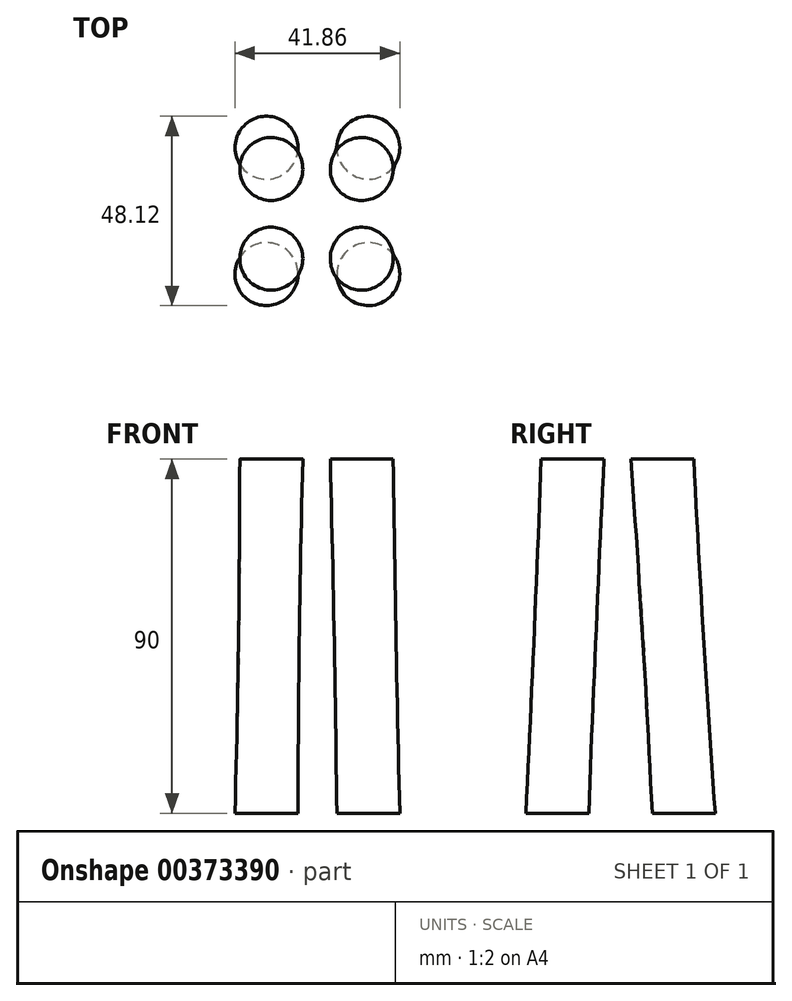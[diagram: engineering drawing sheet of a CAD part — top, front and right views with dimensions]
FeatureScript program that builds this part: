
annotation { "Feature Type Name" : "Feature", "Feature Type Description" : "" }
export const myFeature = defineFeature(function(context is Context, id is Id, definition is map)
    precondition{}
    {
        {
            var Q0;
            Q0=qCreatedBy(makeId("Top.planeOp"),FACE);
            var sketch = newSketch(context, id + "F0", { "sketchPlane" : qUnion([Q0])});
            skCircle(sketch, "E0", {"center": v(0, 0) * mm, "radius": 30 * mm});
            skPoint(sketch, "E1", {"position": v(-13.1, 16.41) * mm});
            skPoint(sketch, "E2", {"position": v(12.76, 16.41) * mm});
            skPoint(sketch, "E3", {"position": v(12.76, -15.71) * mm});
            skPoint(sketch, "E4", {"position": v(-13.1, -15.71) * mm});
            skCircle(sketch, "E5", {"center": v(-13.1, 16.41) * mm, "radius": 8 * mm});
            skCircle(sketch, "E6", {"center": v(12.76, 16.41) * mm, "radius": 8 * mm});
            skCircle(sketch, "E7", {"center": v(12.76, -15.71) * mm, "radius": 8 * mm});
            skCircle(sketch, "E8", {"center": v(-13.1, -15.71) * mm, "radius": 8 * mm});
            skSolve(sketch);
        }
        {
            var Q0;
            Q0=qCreatedBy(makeId("Top.planeOp"),FACE);
            cPlane(context, id + "F1", {"entities" : qUnion([Q0]), "cplaneType" : CPlaneType.OFFSET, "offset" : 90 * mm, "width" : 150 * mm, "height" : 150 * mm});
        }
        {
            var Q0;
            Q0=qCreatedBy(id+"F1.planeOp",FACE);
            var sketch = newSketch(context, id + "F2", { "sketchPlane" : qUnion([Q0])});
            skCircle(sketch, "E9", {"center": v(0, 0) * mm, "radius": 25 * mm});
            skPoint(sketch, "E10", {"position": v(-11.89, 11) * mm});
            skPoint(sketch, "E11", {"position": v(11.1, 11) * mm});
            skPoint(sketch, "E12", {"position": v(11.1, -11.79) * mm});
            skPoint(sketch, "E13", {"position": v(-11.89, -11.79) * mm});
            skCircle(sketch, "E14", {"center": v(-11.89, 11) * mm, "radius": 8 * mm});
            skCircle(sketch, "E15", {"center": v(11.1, 11) * mm, "radius": 8 * mm});
            skCircle(sketch, "E16", {"center": v(11.1, -11.79) * mm, "radius": 8 * mm});
            skCircle(sketch, "E17", {"center": v(-11.89, -11.79) * mm, "radius": 8 * mm});
            skSolve(sketch);
        }
        {
            var Q0;
            Q0=makeQuery(id+"F0.imprint","IMPRINT",FACE,{"disambiguationData":[TD([[makeQuery(id+"F0.imprint","IMPRINT",EDGE,{"derivedFrom":sQuery(id+"F0.wireOp",EDGE,"E7")}),1.0]])]});
            var Q1;
            Q1=makeQuery(id+"F2.imprint","IMPRINT",FACE,{"disambiguationData":[TD([[makeQuery(id+"F2.imprint","IMPRINT",EDGE,{"derivedFrom":sQuery(id+"F2.wireOp",EDGE,"E16")}),1.0]])]});
            loft(context, id + "F3", {"sheetProfilesArray" : [{ "sheetProfileEntities" : qUnion([Q0]) }, { "sheetProfileEntities" : qUnion([Q1]) }]});
        }
        {
            var Q0;
            Q0=makeQuery(id+"F0.imprint","IMPRINT",FACE,{"disambiguationData":[TD([[makeQuery(id+"F0.imprint","IMPRINT",EDGE,{"derivedFrom":sQuery(id+"F0.wireOp",EDGE,"E6")}),1.0]])]});
            var Q1;
            Q1=makeQuery(id+"F2.imprint","IMPRINT",FACE,{"disambiguationData":[TD([[makeQuery(id+"F2.imprint","IMPRINT",EDGE,{"derivedFrom":sQuery(id+"F2.wireOp",EDGE,"E15")}),1.0]])]});
            loft(context, id + "F4", {"sheetProfilesArray" : [{ "sheetProfileEntities" : qUnion([Q0]) }, { "sheetProfileEntities" : qUnion([Q1]) }]});
        }
        {
            var Q0;
            Q0=makeQuery(id+"F0.imprint","IMPRINT",FACE,{"disambiguationData":[TD([[makeQuery(id+"F0.imprint","IMPRINT",EDGE,{"derivedFrom":sQuery(id+"F0.wireOp",EDGE,"E8")}),1.0]])]});
            var Q1;
            Q1=makeQuery(id+"F2.imprint","IMPRINT",FACE,{"disambiguationData":[TD([[makeQuery(id+"F2.imprint","IMPRINT",EDGE,{"derivedFrom":sQuery(id+"F2.wireOp",EDGE,"E17")}),1.0]])]});
            loft(context, id + "F5", {"sheetProfilesArray" : [{ "sheetProfileEntities" : qUnion([Q0]) }, { "sheetProfileEntities" : qUnion([Q1]) }]});
        }
        {
            var Q0;
            Q0=makeQuery(id+"F0.imprint","IMPRINT",FACE,{"disambiguationData":[TD([[makeQuery(id+"F0.imprint","IMPRINT",EDGE,{"derivedFrom":sQuery(id+"F0.wireOp",EDGE,"E5")}),1.0]])]});
            var Q1;
            Q1=makeQuery(id+"F2.imprint","IMPRINT",FACE,{"disambiguationData":[TD([[makeQuery(id+"F2.imprint","IMPRINT",EDGE,{"derivedFrom":sQuery(id+"F2.wireOp",EDGE,"E14")}),1.0]])]});
            loft(context, id + "F6", {"sheetProfilesArray" : [{ "sheetProfileEntities" : qUnion([Q0]) }, { "sheetProfileEntities" : qUnion([Q1]) }]});
        }
        {
            var Q0;
            Q0=makeQuery(id+"F0.imprint","IMPRINT",FACE,{"disambiguationData":[TD([[makeQuery(id+"F0.imprint","IMPRINT",EDGE,{"derivedFrom":sQuery(id+"F0.wireOp",EDGE,"E0")}),1.0]])]});
            var Q1;
            Q1=makeQuery(id+"F2.imprint","IMPRINT",FACE,{"disambiguationData":[TD([[makeQuery(id+"F2.imprint","IMPRINT",EDGE,{"derivedFrom":sQuery(id+"F2.wireOp",EDGE,"E9")}),1.0]])]});
            var Q2;
            Q2=sQuery(id+"F0.wireOp",EDGE,"E0");
            var Q3;
            Q3=sQuery(id+"F2.wireOp",EDGE,"E9");
            loft(context, id + "F7", {"bodyType" : ToolBodyType.SURFACE, "operationType" : NewBodyOperationType.INTERSECT, "sheetProfilesArray" : [{ "sheetProfileEntities" : qUnion([Q0]) }, { "sheetProfileEntities" : qUnion([Q1]) }], "wireProfilesArray" : [{ "wireProfileEntities" : qUnion([Q2]) }, { "wireProfileEntities" : qUnion([Q3]) }]});
        }
    });
